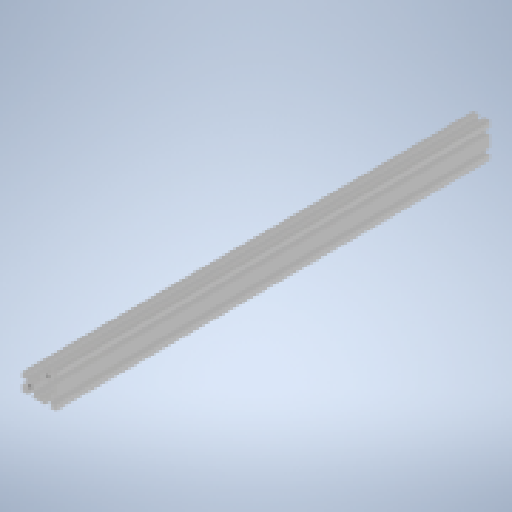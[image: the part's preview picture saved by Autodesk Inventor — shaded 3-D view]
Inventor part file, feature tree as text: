
AUTODESK INVENTOR PART (.ipt)
format: ipt  version: 2024 (Build 280153000, 153)  size: 425,472 bytes
history: native  units: mm
features: thread x4, sketch x3, hole x2, extrude x1
ambient origin geometry x8: Origin, YZ Plane, XZ Plane, XY Plane, X Axis, Y Axis, Z Axis, Center Point
bodies: Solid1 (feature_tree)
feature tree (10):
  extrude  "Extrusion1"  Depth=10.0mm TaperAngle=0.0deg
  hole  "Hole1"  [1 undecoded]
  hole  "Hole2"  [1 undecoded]
  thread  "Thread1"  [1 undecoded]
  thread  "Thread2"  [1 undecoded]
  thread  "Thread3"  [1 undecoded]
  thread  "Thread4"  [1 undecoded]
  sketch  "Sketch_1"  dims[d0=500.0mm d1=0.0mm]
  sketch  "Sketch2"  dims[d2=4.2mm d3=6.0mm d4=4.0mm d5=2.0mm d6=90.0deg d7=425.0mm d8=0.0mm]
  sketch  "Sketch3"  dims[d9=4.2mm d10=6.0mm d11=4.0mm d12=2.0mm d13=90.0deg d14=425.0mm d15=0.0mm d16=10.0mm d17=0.0mm d18=10.0mm d19=0.0mm d20=10.0mm d21=0.0mm d22=10.0mm d23=0.0mm]
note: 6 required parameter values undecoded (feature->parameter linkage not recoverable at this tier; creation-order binding heuristic only, values carry confidence <= 0.55)
